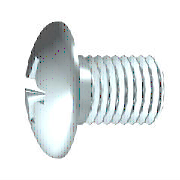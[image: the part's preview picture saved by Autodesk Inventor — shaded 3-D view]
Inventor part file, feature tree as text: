
AUTODESK INVENTOR PART (.ipt)
format: ipt  version: 2015 (Build 190159000, 159)  size: 275,456 bytes
history: native  units: mm (DEFAULTED — no unit token found)
features: sketch x1, plane x1, extrude x1, other x1
ambient origin geometry x7: Origin, YZ Plane, XZ Plane, X Axis, Y Axis, Z Axis, Center Point
bodies: Solid1 (feature_tree), Body (feature_tree)
feature tree (4):
  sketch  "Sketch1"  dims[d1=3.0mm d2=1.96mm d15=90.0deg d3=-2.4mm d4=45.0deg d5=0.966667mm d6=2.9mm d7=0.37mm d8=9.0mm d9=0.0mm d12=10.821041mm d13=4.625123mm d16=2.9mm d17=1.45mm d52=10.0mm d18=0.872665mm d54=90.0deg d19=0.148mm d20=0.0mm d21=3.0mm d22=9.0mm d23=0.306725mm d24=2.4mm d25=5.0mm d27=1.0mm d29=5.6mm d30=10.0mm d72=0.0mm d73=0.0mm d74=0.1mm]
  plane  "Workplane"
  extrude  "Slot"  Depth=0.1mm
  other  "Cut"
